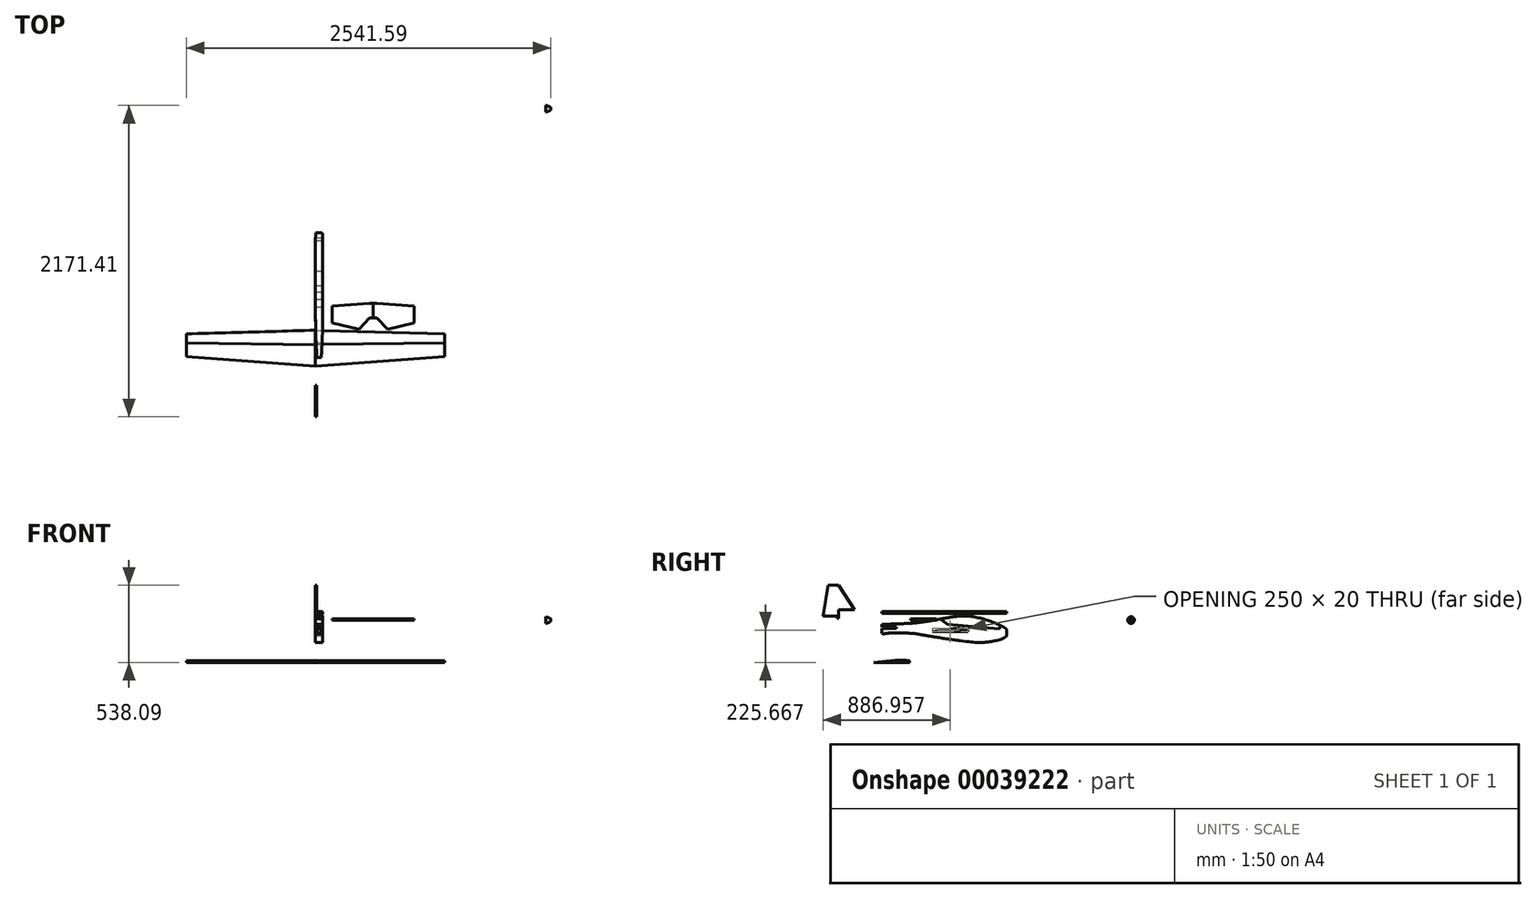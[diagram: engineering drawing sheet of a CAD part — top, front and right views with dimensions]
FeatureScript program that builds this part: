
annotation { "Feature Type Name" : "Feature", "Feature Type Description" : "" }
export const myFeature = defineFeature(function(context is Context, id is Id, definition is map)
    precondition{}
    {
        {
            var Q0;
            Q0=qCreatedBy(makeId("Right.planeOp"),FACE);
            var sketch = newSketch(context, id + "F0", { "sketchPlane" : qUnion([Q0])});
            skLineSegment(sketch, "E0", {"start": v(-360.6, -29.03) * mm, "end": v(519.4, -29.03) * mm});
            skLineSegment(sketch, "E1", {"start": v(-360.6, -29.03) * mm, "end": v(-360.6, -93.09) * mm});
            skFitSpline(sketch, "E2", {"points": [v(519.84, -101.03) * mm, v(398.4, -149.59) * mm, v(266.05, -153.29) * mm, v(-96.57, -100.24) * mm, v(-140.71, -93.09) * mm], "startDerivative": vector(-318.33, -386.55) * mm, "endDerivative": vector(-180.18, 11.6) * mm});
            skFitSpline(sketch, "E3", {"points": [v(519.84, -101.03) * mm, v(519.84, -80.91) * mm, v(487.64, -49.41) * mm, v(272.66, 23.8) * mm, v(90.25, 15.58) * mm, v(-62.17, -11.12) * mm, v(-177.25, -23.17) * mm, v(-360.6, -29.03) * mm], "startDerivative": vector(195.36, 280.51) * mm, "endDerivative": vector(-1108.32, -23.52) * mm});
            skFitSpline(sketch, "E4", {"points": [v(-360.6, -93.09) * mm, v(-331.8, -93.09) * mm, v(-140.71, -93.09) * mm], "startDerivative": vector(72.44, -46.7) * mm, "endDerivative": vector(354.78, -25.1) * mm});
            skLineSegment(sketch, "E5", {"start": v(188.67, 28.12) * mm, "end": v(188.67, -144.45) * mm});
            skLineSegment(sketch, "E6", {"start": v(-360.6, -29.03) * mm, "end": v(-360.6, 58.96) * mm});
            skLineSegment(sketch, "E7", {"start": v(-360.6, 58.96) * mm, "end": v(-42.76, 58.96) * mm});
            skLineSegment(sketch, "E8", {"start": v(-42.76, 58.96) * mm, "end": v(-42.76, 45.6) * mm});
            skLineSegment(sketch, "E9", {"start": v(-42.76, 45.6) * mm, "end": v(-360.6, 45.6) * mm});
            skLineSegment(sketch, "E10", {"start": v(519.14, -79.3) * mm, "end": v(239.14, -79.3) * mm});
            skLineSegment(sketch, "E11", {"start": v(239.14, -79.3) * mm, "end": v(-10.86, -79.3) * mm});
            skLineSegment(sketch, "E12", {"start": v(239.14, -79.3) * mm, "end": v(239.14, -69.3) * mm});
            skLineSegment(sketch, "E13", {"start": v(239.14, -69.3) * mm, "end": v(169.14, -69.3) * mm});
            skLineSegment(sketch, "E14", {"start": v(169.14, -69.3) * mm, "end": v(169.14, -59.3) * mm});
            skLineSegment(sketch, "E15", {"start": v(169.14, -59.3) * mm, "end": v(139.14, -59.3) * mm});
            skLineSegment(sketch, "E16", {"start": v(139.14, -59.3) * mm, "end": v(-10.86, -79.3) * mm});
            skArc(sketch, "E17", {"start": v(239.14, -69.3) * mm, "mid": v(204.5, -61.8) * mm, "end": v(169.14, -59.3) * mm});
            skLineSegment(sketch, "E18", {"start": v(-42.76, 45.6) * mm, "end": v(523.66, 45.6) * mm});
            skLineSegment(sketch, "E19", {"start": v(523.66, 45.6) * mm, "end": v(523.66, 58.96) * mm});
            skLineSegment(sketch, "E20", {"start": v(523.66, 58.96) * mm, "end": v(-42.76, 58.96) * mm});
            skLineSegment(sketch, "E21", {"start": v(-360.6, -29.03) * mm, "end": v(-360.6, -49.03) * mm});
            skLineSegment(sketch, "E22", {"start": v(-360.6, -49.03) * mm, "end": v(-260.6, -49.03) * mm});
            skLineSegment(sketch, "E23", {"start": v(-260.6, -49.03) * mm, "end": v(-260.6, -57.03) * mm});
            skLineSegment(sketch, "E24", {"start": v(-260.6, -57.03) * mm, "end": v(-360.6, -57.03) * mm});
            skLineSegment(sketch, "E25", {"start": v(471.25, -40.37) * mm, "end": v(452.32, -60.38) * mm});
            skLineSegment(sketch, "E26", {"start": v(452.32, -60.38) * mm, "end": v(93.66, -29.03) * mm});
            skLineSegment(sketch, "E27", {"start": v(93.66, -29.03) * mm, "end": v(43.68, 7.21) * mm});
            skSolve(sketch);
        }
        {
            var Q0;
            Q0=qCreatedBy(makeId("Right.planeOp"),FACE);
            var sketch = newSketch(context, id + "F1", { "sketchPlane" : qUnion([Q0])});
            skLineSegment(sketch, "E28", {"start": v(-169.63, -294.96) * mm, "end": v(-169.63, -289.96) * mm});
            skLineSegment(sketch, "E29", {"start": v(-169.63, -289.96) * mm, "end": v(-169.63, -284.96) * mm});
            skLineSegment(sketch, "E30", {"start": v(-239.63, -278.86) * mm, "end": v(-269.63, -278.86) * mm});
            skLineSegment(sketch, "E31", {"start": v(-169.63, -294.96) * mm, "end": v(-419.63, -294.96) * mm});
            skLineSegment(sketch, "E32", {"start": v(-419.63, -294.96) * mm, "end": v(-269.63, -278.86) * mm});
            skArc(sketch, "E33", {"start": v(-169.63, -284.96) * mm, "mid": v(-204.5, -280.39) * mm, "end": v(-239.63, -278.86) * mm});
            skSolve(sketch);
        }
        {
            var Q0;
            Q0=makeQuery(id+"F1.imprint","IMPRINT",FACE,{"disambiguationData":[TD([[makeQuery(id+"F1.imprint","IMPRINT",EDGE,{"derivedFrom":sQuery(id+"F1.wireOp",EDGE,"E28")}),1.0]])]});
            cPlane(context, id + "F2", {"entities" : qUnion([Q0]), "cplaneType" : CPlaneType.OFFSET, "offset" : 900 * mm, "width" : 150 * mm, "height" : 150 * mm});
        }
        {
            var Q0;
            Q0=qCreatedBy(id+"F2.planeOp",FACE);
            var sketch = newSketch(context, id + "F3", { "sketchPlane" : qUnion([Q0])});
            skLineSegment(sketch, "E34", {"start": v(-169.48, -294.88) * mm, "end": v(-169.48, -289.88) * mm});
            skLineSegment(sketch, "E35", {"start": v(-169.48, -289.88) * mm, "end": v(-169.48, -284.88) * mm});
            skLineSegment(sketch, "E36", {"start": v(-169.48, -294.88) * mm, "end": v(-194.48, -294.88) * mm});
            skLineSegment(sketch, "E37", {"start": v(-194.48, -294.88) * mm, "end": v(-194.48, -288.88) * mm});
            skLineSegment(sketch, "E38", {"start": v(-239.48, -281.88) * mm, "end": v(-259.48, -281.88) * mm});
            skLineSegment(sketch, "E39", {"start": v(-194.48, -294.88) * mm, "end": v(-354.48, -294.88) * mm});
            skLineSegment(sketch, "E40", {"start": v(-259.48, -281.88) * mm, "end": v(-354.48, -294.88) * mm});
            skArc(sketch, "E41", {"start": v(-194.48, -288.88) * mm, "mid": v(-216.7, -283.64) * mm, "end": v(-239.48, -281.88) * mm});
            skSolve(sketch);
        }
        {
            var Q0;
            Q0=makeQuery(id+"F1.imprint","IMPRINT",FACE,{"disambiguationData":[TD([[makeQuery(id+"F1.imprint","IMPRINT",EDGE,{"derivedFrom":sQuery(id+"F1.wireOp",EDGE,"E28")}),1.0]])]});
            var Q1;
            Q1=makeQuery(id+"F3.imprint","IMPRINT",FACE,{"disambiguationData":[TD([[makeQuery(id+"F3.imprint","IMPRINT",EDGE,{"derivedFrom":sQuery(id+"F3.wireOp",EDGE,"E37")}),1.0]])]});
            loft(context, id + "F4", {"sheetProfilesArray" : [{ "sheetProfileEntities" : qUnion([Q0]) }, { "sheetProfileEntities" : qUnion([Q1]) }]});
        }
        {
            var Q0;
            {var subQ8=sQuery(id+"F0.wireOp",EDGE,"E10");Q0=makeQuery(id+"F0.imprint","IMPRINT",FACE,{"disambiguationData":[TD([[makeQuery(id+"F0.imprint","IMPRINT",EDGE,{"derivedFrom":subQ8}),-1.0]])]});}
            var Q1;
            {var subQ3=sQuery(id+"F0.wireOp",EDGE,"E10");Q1=makeQuery(id+"F0.imprint","IMPRINT",FACE,{"disambiguationData":[TD([[makeQuery(id+"F0.imprint","IMPRINT",EDGE,{"derivedFrom":subQ3}),1.0]])]});}
            var Q2;
            Q2=makeQuery(id+"F0.imprint","IMPRINT",FACE,{"disambiguationData":[TD([[makeQuery(id+"F0.imprint","IMPRINT",EDGE,{"derivedFrom":sQuery(id+"F0.wireOp",EDGE,"E8")}),1.0]])]});
            var Q3;
            {var subQ1=sQuery(id+"F0.wireOp",EDGE,"E7");Q3=makeQuery(id+"F0.imprint","IMPRINT",FACE,{"disambiguationData":[TD([[makeQuery(id+"F0.imprint","IMPRINT",EDGE,{"derivedFrom":subQ1}),-1.0]])]});}
            var Q4;
            {var subQ0=sQuery(id+"F0.wireOp",EDGE,"E4");Q4=makeQuery(id+"F0.imprint","IMPRINT",FACE,{"disambiguationData":[TD([[makeQuery(id+"F0.imprint","IMPRINT",EDGE,{"derivedFrom":subQ0}),1.0]])]});}
            var Q5;
            {var subQ0=sQuery(id+"F0.wireOp",EDGE,"E27");Q5=makeQuery(id+"F0.imprint","IMPRINT",FACE,{"disambiguationData":[TD([[makeQuery(id+"F0.imprint","IMPRINT",EDGE,{"derivedFrom":subQ0}),1.0]])]});}
            extrude(context, id + "F5", {"entities" : qUnion([Q0, Q1, Q2, Q3, Q4, Q5]), "depth" : 50 * mm});
        }
        {
            var Q0;
            Q0=makeQuery(id+"F5.opExtrude","SWEPT_FACE",FACE,{"disambiguationData":[OSD([sQuery(id+"F0.wireOp",EDGE,"E7"),sQuery(id+"F0.wireOp",EDGE,"E20")])]});
            var sketch = newSketch(context, id + "F6", { "sketchPlane" : qUnion([Q0])});
            skLineSegment(sketch, "E42", {"start": v(50, 523.66) * mm, "end": v(50, 483.66) * mm});
            skLineSegment(sketch, "E43", {"start": v(0, 523.66) * mm, "end": v(0, 483.66) * mm});
            skLineSegment(sketch, "E44", {"start": v(25, 523.66) * mm, "end": v(33, 523.66) * mm});
            skLineSegment(sketch, "E45", {"start": v(25, 523.66) * mm, "end": v(17, 523.66) * mm});
            skArc(sketch, "E46", {"start": v(50, 483.66) * mm, "mid": v(45.57, 505.39) * mm, "end": v(33, 523.66) * mm});
            skArc(sketch, "E47", {"start": v(17, 523.66) * mm, "mid": v(4.43, 505.39) * mm, "end": v(0, 483.66) * mm});
            skLineSegment(sketch, "E48", {"start": v(50, -360.6) * mm, "end": v(50, -60.6) * mm});
            skLineSegment(sketch, "E49", {"start": v(50, -60.6) * mm, "end": v(0, -60.6) * mm});
            skLineSegment(sketch, "E50", {"start": v(0, -360.6) * mm, "end": v(10, -360.6) * mm});
            skLineSegment(sketch, "E51", {"start": v(50, -360.6) * mm, "end": v(40, -360.6) * mm});
            skArc(sketch, "E52", {"start": v(40, -360.6) * mm, "mid": v(47.5, -210.7) * mm, "end": v(50, -60.6) * mm});
            skLineSegment(sketch, "E53", {"start": v(0, -60.6) * mm, "end": v(0, -360.6) * mm});
            skArc(sketch, "E54", {"start": v(0, -60.6) * mm, "mid": v(2.5, -210.7) * mm, "end": v(10, -360.6) * mm});
            skLineSegment(sketch, "E55", {"start": v(25, 523.66) * mm, "end": v(25, 508.66) * mm});
            skLineSegment(sketch, "E56", {"start": v(25, 508.66) * mm, "end": v(47.5, 508.66) * mm});
            skLineSegment(sketch, "E57", {"start": v(25, 508.66) * mm, "end": v(2.5, 508.66) * mm});
            skLineSegment(sketch, "E58", {"start": v(47.5, 508.66) * mm, "end": v(47.5, 468.66) * mm});
            skLineSegment(sketch, "E59", {"start": v(2.5, 508.66) * mm, "end": v(2.5, 468.66) * mm});
            skLineSegment(sketch, "E60", {"start": v(2.5, 468.66) * mm, "end": v(0, 468.66) * mm});
            skLineSegment(sketch, "E61", {"start": v(47.5, 468.66) * mm, "end": v(50, 468.66) * mm});
            skLineSegment(sketch, "E62", {"start": v(50, 468.66) * mm, "end": v(50, 483.66) * mm});
            skArc(sketch, "E63", {"start": v(50, 468.66) * mm, "mid": v(49.37, 488.7) * mm, "end": v(47.5, 508.66) * mm});
            skLineSegment(sketch, "E64", {"start": v(0, 483.66) * mm, "end": v(0, 468.66) * mm});
            skArc(sketch, "E65", {"start": v(2.5, 508.66) * mm, "mid": v(0.63, 488.7) * mm, "end": v(0, 468.66) * mm});
            skSolve(sketch);
        }
        {
            var Q0;
            Q0=makeQuery(id+"F6.imprint","IMPRINT",FACE,{"disambiguationData":[TD([[makeQuery(id+"F6.imprint","IMPRINT",EDGE,{"derivedFrom":sQuery(id+"F6.wireOp",EDGE,"E48")}),-1.0]])]});
            var Q1;
            Q1=makeQuery(id+"F6.imprint","IMPRINT",FACE,{"disambiguationData":[TD([[makeQuery(id+"F6.imprint","IMPRINT",EDGE,{"derivedFrom":sQuery(id+"F6.wireOp",EDGE,"E50")}),-1.0]])]});
            var Q2;
            {var subQ2=sQuery(id+"F6.wireOp",EDGE,"E42");Q2=makeQuery(id+"F6.imprint","IMPRINT",FACE,{"disambiguationData":[TD([[makeQuery(id+"F6.imprint","IMPRINT",EDGE,{"derivedFrom":subQ2}),-1.0]])]});}
            var Q3;
            {var subQ2=sQuery(id+"F6.wireOp",EDGE,"E43");Q3=makeQuery(id+"F6.imprint","IMPRINT",FACE,{"disambiguationData":[TD([[makeQuery(id+"F6.imprint","IMPRINT",EDGE,{"derivedFrom":subQ2}),1.0]])]});}
            var Q4;
            Q4=makeQuery(id+"F6.imprint","IMPRINT",FACE,{"disambiguationData":[TD([[makeQuery(id+"F6.imprint","IMPRINT",EDGE,{"derivedFrom":sQuery(id+"F6.wireOp",EDGE,"E45")}),1.0]])]});
            var Q5;
            Q5=makeQuery(id+"F6.imprint","IMPRINT",FACE,{"disambiguationData":[TD([[makeQuery(id+"F6.imprint","IMPRINT",EDGE,{"derivedFrom":sQuery(id+"F6.wireOp",EDGE,"E44")}),1.0]])]});
            var Q6;
            {var subQ3=sQuery(id+"F6.wireOp",EDGE,"E62");Q6=makeQuery(id+"F6.imprint","IMPRINT",FACE,{"disambiguationData":[TD([[makeQuery(id+"F6.imprint","IMPRINT",EDGE,{"derivedFrom":subQ3}),-1.0]])]});}
            var Q7;
            {var subQ3=sQuery(id+"F6.wireOp",EDGE,"E64");Q7=makeQuery(id+"F6.imprint","IMPRINT",FACE,{"disambiguationData":[TD([[makeQuery(id+"F6.imprint","IMPRINT",EDGE,{"derivedFrom":subQ3}),1.0]])]});}
            extrude(context, id + "F7", {"entities" : qUnion([Q0, Q1, Q2, Q3, Q4, Q5, Q6, Q7]), "operationType" : NewBodyOperationType.REMOVE, "oppositeDirection" : true, "depth" : 200 * mm});
        }
        {
            var Q0;
            Q0=makeQuery(id+"F4.opLoft","SWEPT_BODY",BODY,{"disambiguationData":[OSD([makeQuery(id+"F1.imprint","IMPRINT",FACE,{"disambiguationData":[TD([[makeQuery(id+"F1.imprint","IMPRINT",EDGE,{"derivedFrom":sQuery(id+"F1.wireOp",EDGE,"E28")}),1.0]])]}),makeQuery(id+"F3.imprint","IMPRINT",FACE,{"disambiguationData":[TD([[makeQuery(id+"F3.imprint","IMPRINT",EDGE,{"derivedFrom":sQuery(id+"F3.wireOp",EDGE,"E37")}),1.0]])]})])]});
            var Q1;
            Q1=makeQuery(id+"F1.imprint","IMPRINT",FACE,{"disambiguationData":[TD([[makeQuery(id+"F1.imprint","IMPRINT",EDGE,{"derivedFrom":sQuery(id+"F1.wireOp",EDGE,"E28")}),1.0]])]});
            mirror(context, id + "F8", {"entities" : qUnion([Q0]), "mirrorPlane" : qUnion([Q1])});
        }
        {
            var Q0;
            Q0=qCreatedBy(makeId("Top.planeOp"),FACE);
            var sketch = newSketch(context, id + "F9", { "sketchPlane" : qUnion([Q0])});
            skLineSegment(sketch, "E66", {"start": v(427.29, 18) * mm, "end": v(427.29, -82) * mm});
            skLineSegment(sketch, "E67", {"start": v(427.29, -82) * mm, "end": v(402.29, -82) * mm});
            skLineSegment(sketch, "E68", {"start": v(402.29, -82) * mm, "end": v(402.29, 18) * mm});
            skLineSegment(sketch, "E69", {"start": v(402.29, 18) * mm, "end": v(427.29, 18) * mm});
            skLineSegment(sketch, "E70", {"start": v(427.29, 18) * mm, "end": v(687.29, 18) * mm});
            skLineSegment(sketch, "E71", {"start": v(687.29, 18) * mm, "end": v(687.29, 0) * mm});
            skLineSegment(sketch, "E72", {"start": v(687.29, 0) * mm, "end": v(687.29, -120) * mm});
            skLineSegment(sketch, "E73", {"start": v(427.29, 18) * mm, "end": v(427.29, -162) * mm});
            skLineSegment(sketch, "E74", {"start": v(427.29, -162) * mm, "end": v(502.29, -162) * mm});
            skLineSegment(sketch, "E75", {"start": v(502.29, -162) * mm, "end": v(687.29, -120) * mm});
            skLineSegment(sketch, "E76", {"start": v(687.29, 0) * mm, "end": v(427.29, 18) * mm});
            skLineSegment(sketch, "E77", {"start": v(427.29, -82) * mm, "end": v(502.29, -162) * mm});
            skSolve(sketch);
        }
        {
            var Q0;
            {var subQ2=sQuery(id+"F9.wireOp",EDGE,"E67");Q0=makeQuery(id+"F9.imprint","IMPRINT",FACE,{"disambiguationData":[TD([[makeQuery(id+"F9.imprint","IMPRINT",EDGE,{"derivedFrom":subQ2}),-1.0]])]});}
            var Q1;
            Q1=makeQuery(id+"F9.imprint","IMPRINT",FACE,{"disambiguationData":[TD([[makeQuery(id+"F9.imprint","IMPRINT",EDGE,{"derivedFrom":sQuery(id+"F9.wireOp",EDGE,"E72")}),-1.0]])]});
            extrude(context, id + "F10", {"entities" : qUnion([Q0, Q1]), "depth" : 8 * mm});
        }
        {
            var Q0;
            Q0=makeQuery(id+"F10.opExtrude","SWEPT_BODY",BODY,{"disambiguationData":[OSD([sQuery(id+"F9.wireOp",EDGE,"E67"),sQuery(id+"F9.wireOp",EDGE,"E68"),sQuery(id+"F9.wireOp",EDGE,"E69"),sQuery(id+"F9.wireOp",EDGE,"E72"),sQuery(id+"F9.wireOp",EDGE,"E75"),sQuery(id+"F9.wireOp",EDGE,"E76"),sQuery(id+"F9.wireOp",EDGE,"E77")])]});
            var Q1;
            Q1=makeQuery(id+"F10.opExtrude","SWEPT_FACE",FACE,{"disambiguationData":[OSD([sQuery(id+"F9.wireOp",EDGE,"E68")])]});
            mirror(context, id + "F11", {"operationType" : NewBodyOperationType.ADD, "entities" : qUnion([Q0]), "mirrorPlane" : qUnion([Q1])});
        }
        {
            var Q0;
            {var subQ1=sQuery(id+"F0.wireOp",EDGE,"E0");var subQ3=sQuery(id+"F0.wireOp",EDGE,"E3");var subQ5=makeQuery(id+"F0.imprint","INTERSECT",VERTEX,{"derivedFrom":[subQ1,subQ3]});Q0=makeQuery(id+"F0.imprint","IMPRINT",FACE,{"disambiguationData":[TD([[makeQuery(id+"F0.imprint","IMPRINT",EDGE,{"disambiguationData":[TD([[subQ5,1.0]])],"derivedFrom":subQ1}),1.0]])]});}
            var Q1;
            {var subQ0=sQuery(id+"F0.wireOp",EDGE,"E27");Q1=makeQuery(id+"F0.imprint","IMPRINT",FACE,{"disambiguationData":[TD([[makeQuery(id+"F0.imprint","IMPRINT",EDGE,{"derivedFrom":subQ0}),-1.0]])]});}
            var Q2;
            {var subQ3=sQuery(id+"F0.wireOp",EDGE,"E25");Q2=makeQuery(id+"F0.imprint","IMPRINT",FACE,{"disambiguationData":[TD([[makeQuery(id+"F0.imprint","IMPRINT",EDGE,{"derivedFrom":subQ3}),-1.0]])]});}
            var Q3;
            {var subQ1=sQuery(id+"F0.wireOp",EDGE,"E5");var subQ3=sQuery(id+"F0.wireOp",EDGE,"E0");var subQ5=makeQuery(id+"F0.imprint","INTERSECT",VERTEX,{"derivedFrom":[subQ3,subQ1]});Q3=makeQuery(id+"F0.imprint","IMPRINT",FACE,{"disambiguationData":[TD([[makeQuery(id+"F0.imprint","IMPRINT",EDGE,{"disambiguationData":[TD([[subQ5,-1.0]])],"derivedFrom":subQ1}),-1.0]])]});}
            extrude(context, id + "F12", {"entities" : qUnion([Q0, Q1, Q2, Q3]), "depth" : 50 * mm});
        }
        {
            var Q0;
            Q0=qCreatedBy(makeId("Right.planeOp"),FACE);
            var sketch = newSketch(context, id + "F13", { "sketchPlane" : qUnion([Q0])});
            skLineSegment(sketch, "E78", {"start": v(-662.82, 243.13) * mm, "end": v(-672.82, 243.13) * mm});
            skLineSegment(sketch, "E79", {"start": v(-672.82, 243.13) * mm, "end": v(-737.82, 243.13) * mm});
            skLineSegment(sketch, "E80", {"start": v(-672.82, 243.13) * mm, "end": v(-672.82, 13.13) * mm});
            skLineSegment(sketch, "E81", {"start": v(-672.82, 13.13) * mm, "end": v(-662.82, 13.13) * mm});
            skLineSegment(sketch, "E82", {"start": v(-672.82, 13.13) * mm, "end": v(-672.82, 28.13) * mm});
            skLineSegment(sketch, "E83", {"start": v(-672.82, 28.13) * mm, "end": v(-772.82, 28.13) * mm});
            skLineSegment(sketch, "E84", {"start": v(-737.82, 243.13) * mm, "end": v(-772.82, 28.13) * mm});
            skLineSegment(sketch, "E85", {"start": v(-772.82, 28.13) * mm, "end": v(-672.82, 13.13) * mm});
            skLineSegment(sketch, "E86", {"start": v(-662.82, 13.13) * mm, "end": v(-662.82, 73.13) * mm});
            skLineSegment(sketch, "E87", {"start": v(-662.82, 73.13) * mm, "end": v(-552.82, 73.13) * mm});
            skLineSegment(sketch, "E88", {"start": v(-662.82, 243.13) * mm, "end": v(-552.82, 73.13) * mm});
            skSolve(sketch);
        }
        {
            var Q0;
            Q0=makeQuery(id+"F13.imprint","IMPRINT",FACE,{"disambiguationData":[TD([[makeQuery(id+"F13.imprint","IMPRINT",EDGE,{"derivedFrom":sQuery(id+"F13.wireOp",EDGE,"E78")}),1.0]])]});
            var Q1;
            Q1=makeQuery(id+"F13.imprint","IMPRINT",FACE,{"disambiguationData":[TD([[makeQuery(id+"F13.imprint","IMPRINT",EDGE,{"derivedFrom":sQuery(id+"F13.wireOp",EDGE,"E79")}),1.0]])]});
            var Q2;
            Q2=makeQuery(id+"F13.imprint","IMPRINT",FACE,{"disambiguationData":[TD([[makeQuery(id+"F13.imprint","IMPRINT",EDGE,{"derivedFrom":sQuery(id+"F13.wireOp",EDGE,"E82")}),1.0]])]});
            extrude(context, id + "F14", {"entities" : qUnion([Q0, Q1, Q2]), "depth" : 8 * mm});
        }
        {
            var Q0;
            Q0=qCreatedBy(makeId("Top.planeOp"),FACE);
            var sketch = newSketch(context, id + "F15", { "sketchPlane" : qUnion([Q0])});
            skLineSegment(sketch, "E89", {"start": v(1603.8, 1375.1) * mm, "end": v(1603.8, 1398.6) * mm});
            skLineSegment(sketch, "E90", {"start": v(1603.8, 1375.1) * mm, "end": v(1641.6, 1375.1) * mm});
            skLineSegment(sketch, "E91", {"start": v(1641.6, 1375.1) * mm, "end": v(1641.6, 1383.1) * mm});
            skArc(sketch, "E92", {"start": v(1641.6, 1383.1) * mm, "mid": v(1623.46, 1392.71) * mm, "end": v(1603.8, 1398.6) * mm});
            skSolve(sketch);
        }
        {
            var Q0;
            Q0=makeQuery(id+"F15.imprint","IMPRINT",FACE,{"disambiguationData":[TD([[makeQuery(id+"F15.imprint","IMPRINT",EDGE,{"derivedFrom":sQuery(id+"F15.wireOp",EDGE,"E89")}),-1.0]])]});
            var Q1;
            Q1=sQuery(id+"F15.wireOp",EDGE,"E90");
            revolve(context, id + "F16", {"entities" : qUnion([Q0]), "axis" : qUnion([Q1]), "revolveType" : RevolveType.FULL});
        }
    });
